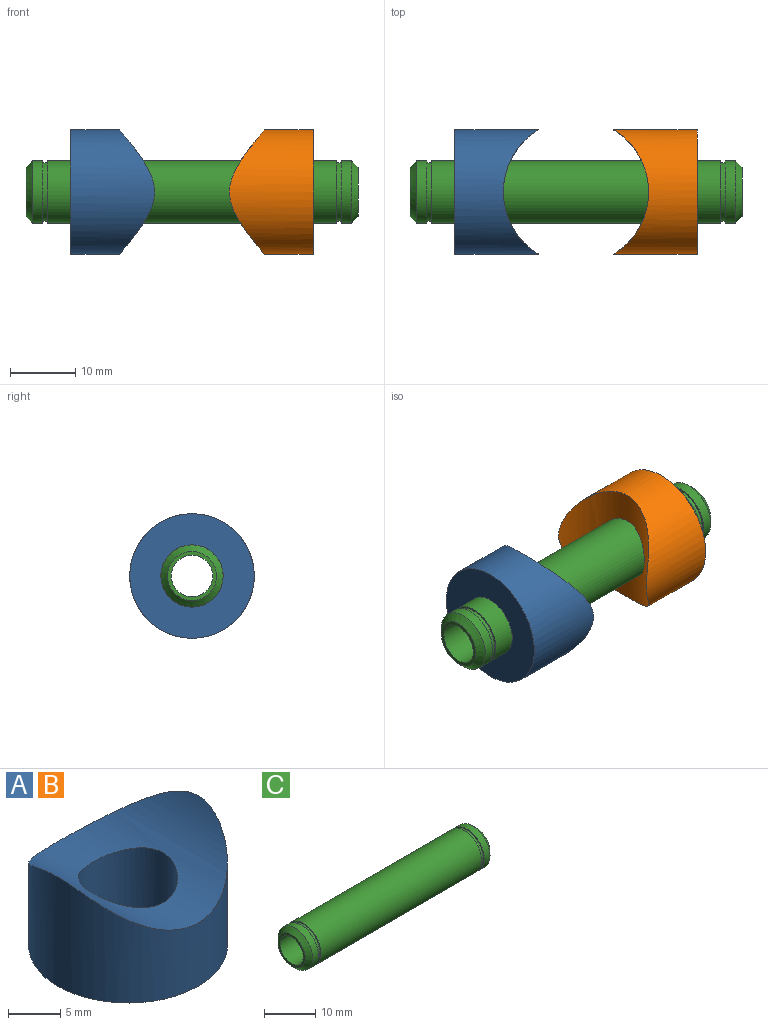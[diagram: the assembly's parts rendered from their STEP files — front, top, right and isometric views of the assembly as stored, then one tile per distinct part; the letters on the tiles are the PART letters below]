
ASSEMBLY  parts=3 mates=3
PART A: 4 faces, bbox 19.1x19.1x12.8 mm
  f0: cylinder r=9.53mm len=19.05mm, axis (0,0,1), area 592.7mm2, adj f2,f3
  f1: cylinder r=4.76mm len=9.53mm, axis (0,0,1), area 238.2mm2, adj f2,f3
  f2: plane 19.05x19.05mm, normal (0,0,-1), area 213.8mm2, adj f0,f1
  f3: cylinder r=11.11mm len=19.05mm, axis (0,1,0), area 250.5mm2, adj f0,f1
PART B: same geometry as A
PART C: 14 faces, bbox 50.8x9.5x9.5 mm
  f0: cylinder r=4.76mm len=44.2mm, axis (-1,0,0), area 1322.5mm2, adj f8,f9
  f1: cylinder r=4.76mm len=9.53mm, axis (-1,0,0), area 46.4mm2, adj f10,f13
  f2: cylinder r=4.76mm len=9.53mm, axis (-1,0,0), area 46.4mm2, adj f6,f12
  f3: plane 7.49x7.49mm, normal (1,0,0), area 12.4mm2, adj f5,f12
  f4: plane 7.49x7.49mm, normal (-1,0,0), area 12.4mm2, adj f5,f13
  f5: cylinder r=3.17mm len=50.8mm, axis (-1,0,0), area 1013.4mm2, adj f3,f4
  f6: plane 9.53x9.53mm, normal (-1,0,0), area 8.5mm2, adj f2,f7
  f7: cylinder r=4.47mm len=8.94mm, axis (-1,0,0), area 20.7mm2, adj f6,f8
  f8: plane 9.53x9.53mm, normal (1,0,0), area 8.5mm2, adj f0,f7
  f9: plane 9.53x9.53mm, normal (-1,0,0), area 8.5mm2, adj f0,f11
  f10: plane 9.53x9.53mm, normal (1,0,0), area 8.5mm2, adj f1,f11
  f11: cylinder r=4.47mm len=8.94mm, axis (-1,0,0), area 20.7mm2, adj f9,f10
  f12: cone r=3.75mm half-angle=45deg, axis (-1,0,0), area 38.4mm2, adj f2,f3
  f13: cone r=4.76mm half-angle=45deg, axis (1,0,0), area 38.4mm2, adj f1,f4
PLACE A rot(axis=(0.58,0.58,0.58),120deg) t=(-5.72,0,0)mm
PLACE B rot(axis=(0.58,-0.58,-0.58),120deg) t=(5.72,0,0)mm
PLACE C rot(axis=(0,1,0),180deg) t=(0,0,0)mm fixed
MATE cylindrical A.f3 <-> B.f3  axis (0,0,1) through (0,0,0)mm
MATE cylindrical B.f0 <-> C.f0  axis (-1,0,0) through (18.54,0,0)mm
MATE cylindrical A.f0 <-> C.f0  axis (1,0,0) through (-18.54,0,0)mm
